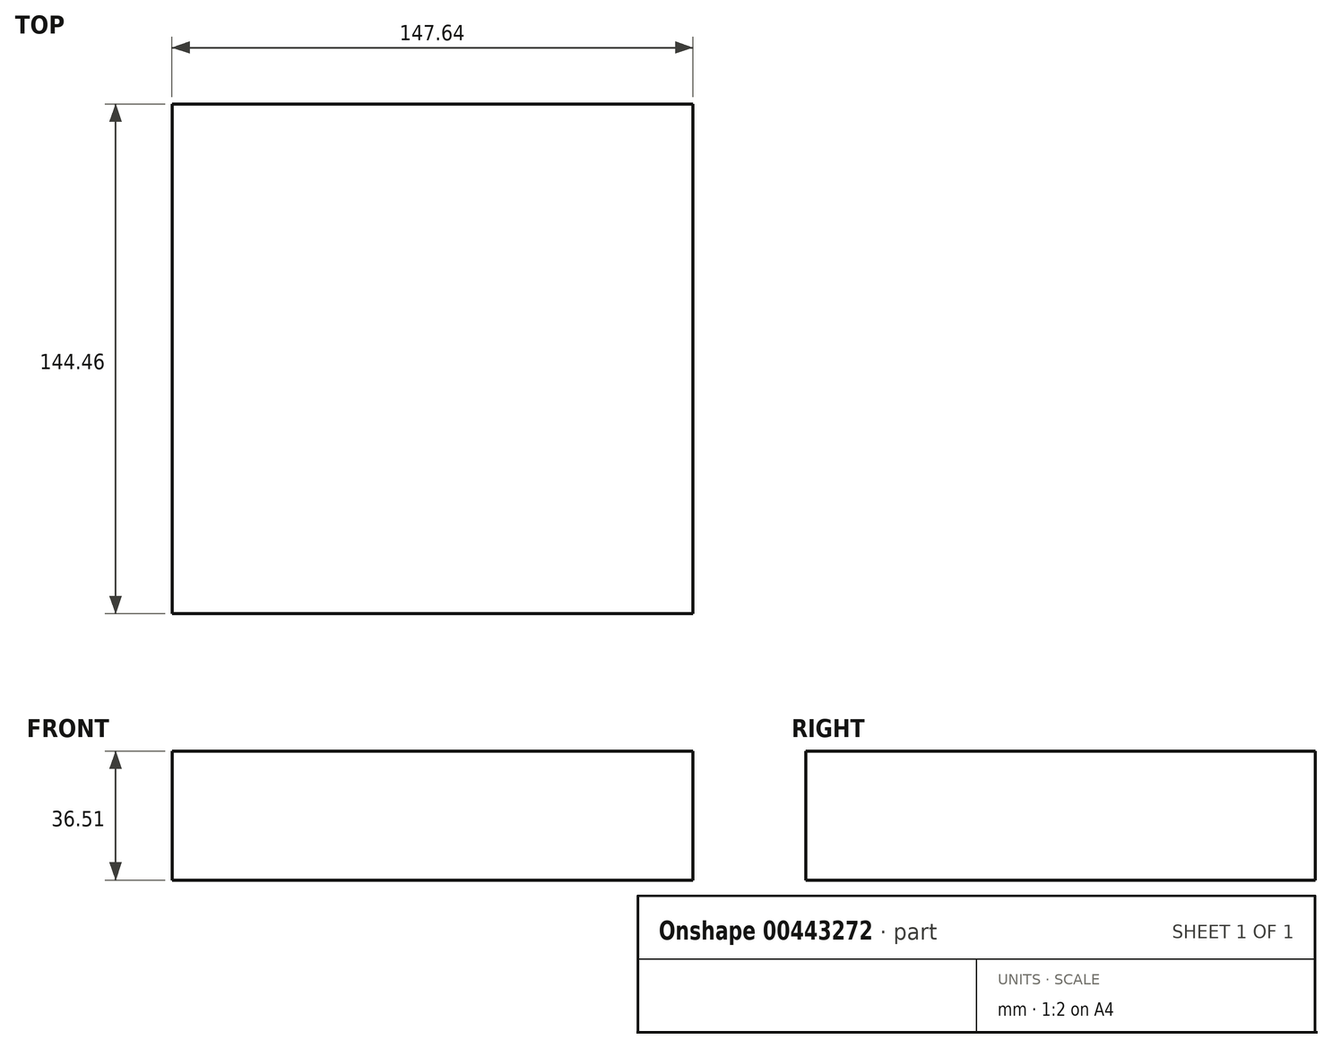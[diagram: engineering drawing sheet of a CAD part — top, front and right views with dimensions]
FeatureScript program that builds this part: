
annotation { "Feature Type Name" : "Feature", "Feature Type Description" : "" }
export const myFeature = defineFeature(function(context is Context, id is Id, definition is map)
    precondition{}
    {
        {
            var Q0;
            Q0=qCreatedBy(makeId("Top.planeOp"),FACE);
            var sketch = newSketch(context, id + "F0", { "sketchPlane" : qUnion([Q0])});
            skLineSegment(sketch, "E0.bottom", {"start": v(73.82, -72.23) * mm, "end": v(-73.82, -72.23) * mm});
            skLineSegment(sketch, "E0.top", {"start": v(73.82, 72.23) * mm, "end": v(-73.82, 72.23) * mm});
            skLineSegment(sketch, "E0.left", {"start": v(73.82, -72.23) * mm, "end": v(73.82, 72.23) * mm});
            skLineSegment(sketch, "E0.right", {"start": v(-73.82, -72.23) * mm, "end": v(-73.82, 72.23) * mm});
            skPoint(sketch, "E0.middle", {"position": v(0, 0) * mm});
            skSolve(sketch);
        }
        {
            var Q0;
            Q0=makeQuery(id+"F0.imprint","IMPRINT",FACE,{"disambiguationData":[TD([[makeQuery(id+"F0.imprint","IMPRINT",EDGE,{"derivedFrom":sQuery(id+"F0.wireOp",EDGE,"E0.bottom")}),-1.0]])]});
            extrude(context, id + "F1", {"entities" : qUnion([Q0]), "depth" : 36.5 * mm});
        }
    });
